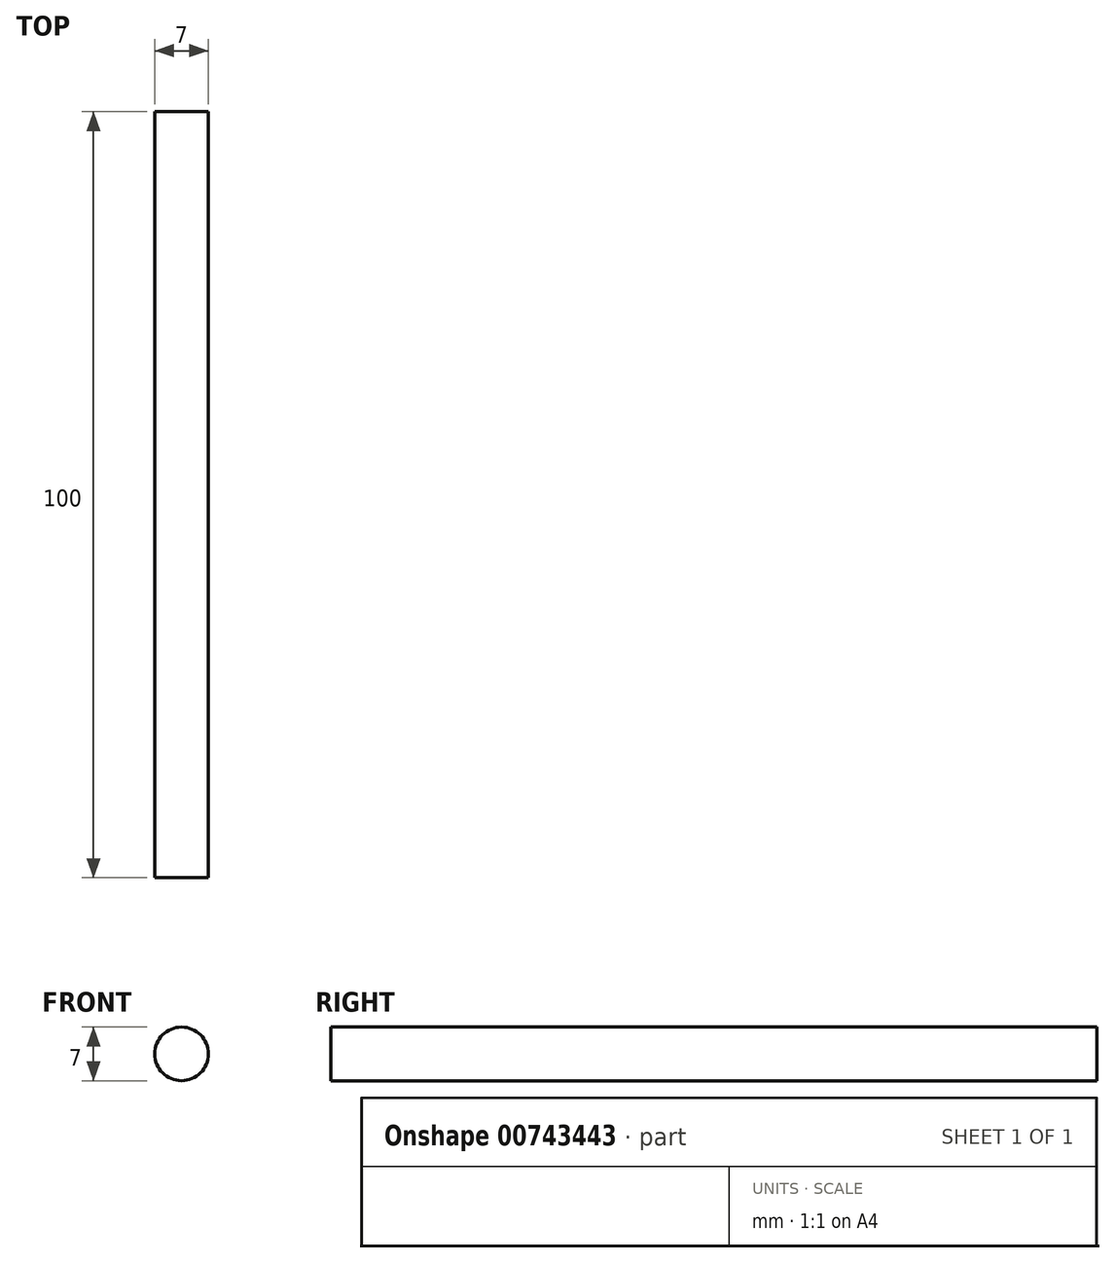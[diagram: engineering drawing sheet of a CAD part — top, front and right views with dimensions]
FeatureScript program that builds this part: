
annotation { "Feature Type Name" : "Feature", "Feature Type Description" : "" }
export const myFeature = defineFeature(function(context is Context, id is Id, definition is map)
    precondition{}
    {
        {
            var Q0;
            Q0=qCreatedBy(makeId("Front.planeOp"),FACE);
            var sketch = newSketch(context, id + "F0", { "sketchPlane" : qUnion([Q0])});
            skCircle(sketch, "E0", {"center": v(0, 0) * mm, "radius": 3.5 * mm});
            skSolve(sketch);
        }
        {
            var Q0;
            Q0=qSketchRegion(id+"F0",true);
            extrude(context, id + "F1", {"entities" : qUnion([Q0]), "depth" : 100 * mm, "offsetDistance" : 25 * mm});
        }
    });
